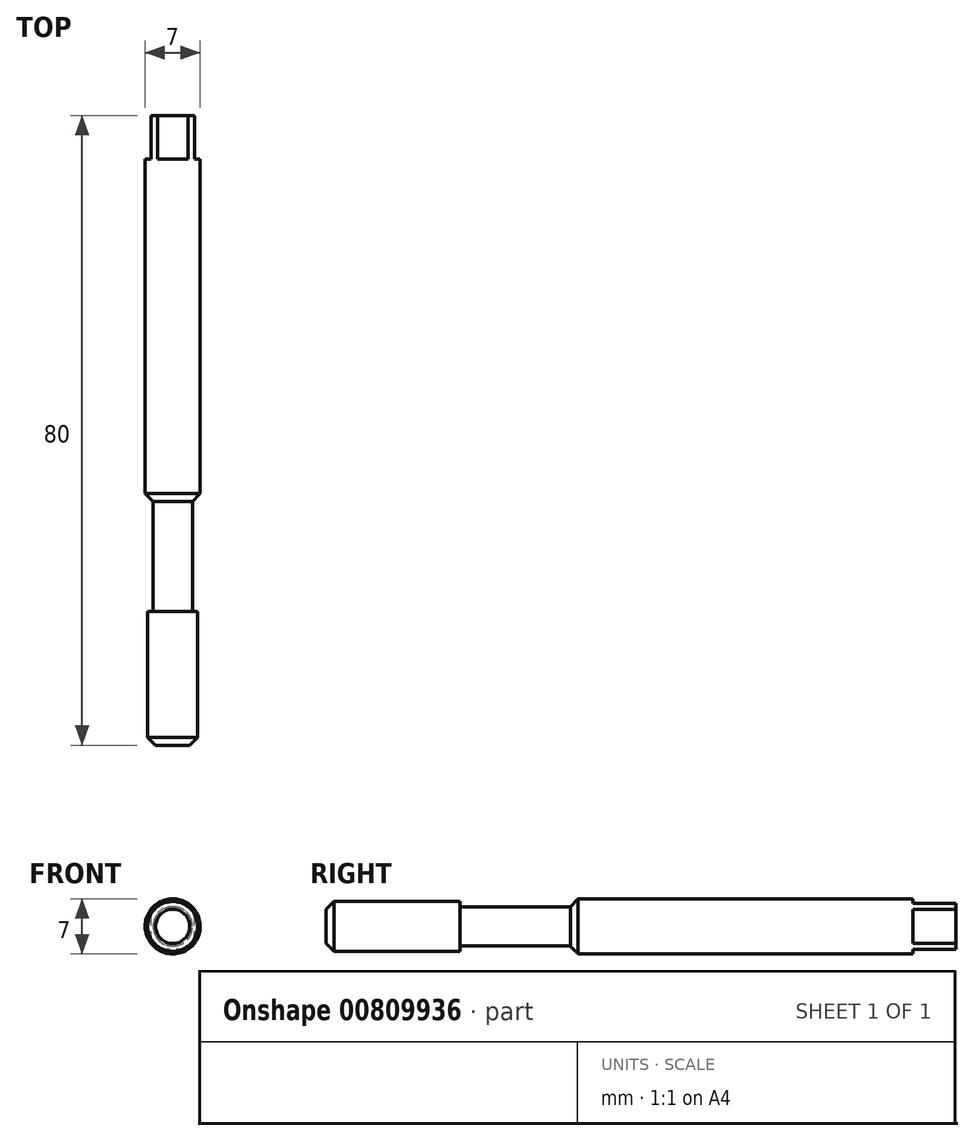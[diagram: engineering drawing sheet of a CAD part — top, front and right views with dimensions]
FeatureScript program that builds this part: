
annotation { "Feature Type Name" : "Feature", "Feature Type Description" : "" }
export const myFeature = defineFeature(function(context is Context, id is Id, definition is map)
    precondition{}
    {
        {
            var Q0;
            Q0=qCreatedBy(makeId("Front.planeOp"),FACE);
            var sketch = newSketch(context, id + "F0", { "sketchPlane" : qUnion([Q0])});
            skCircle(sketch, "E0", {"center": v(0, 0) * mm, "radius": 3.5 * mm});
            skSolve(sketch);
        }
        {
            var Q0;
            Q0 = qSketchRegion(id + "F0", true);
            extrude(context, id + "F1", {"entities" : qUnion([Q0]), "depth" : 80 * mm, "offsetDistance" : 25 * mm});
        }
        {
            var Q0;
            Q0=makeQuery(id+"F1.opExtrude","CAP_FACE",FACE,{"disambiguationData":[OSD([sQuery(id+"F0.wireOp",EDGE,"E0")])],"isStart":false});
            var sketch = newSketch(context, id + "F2", { "sketchPlane" : qUnion([Q0])});
            skCircle(sketch, "E1", {"center": v(0, 0) * mm, "radius": 2.5 * mm});
            skCircle(sketch, "E2", {"center": v(0, 0) * mm, "radius": 6.33 * mm});
            skSolve(sketch);
        }
        {
            var Q0;
            Q0 = qSketchRegion(id + "F2", true);
            extrude(context, id + "F3", {"entities" : qUnion([Q0]), "operationType" : NewBodyOperationType.REMOVE, "oppositeDirection" : true, "depth" : 30 * mm, "offsetDistance" : 25 * mm});
        }
        {
            var Q0;
            Q0=makeQuery(id+"F3.boolean.opBoolean","INTERSECT",EDGE,{"derivedFrom":[makeQuery(id+"F1.opExtrude","SWEPT_FACE",FACE,{"disambiguationData":[OSD([sQuery(id+"F0.wireOp",EDGE,"E0")])]}),makeQuery(id+"F3.opExtrude","CAP_FACE",FACE,{"disambiguationData":[OSD([sQuery(id+"F2.wireOp",EDGE,"E1"),sQuery(id+"F2.wireOp",EDGE,"E2")])],"isStart":false})]});
            chamfer(context, id + "F4", {"entities" : qUnion([Q0]), "width" : 2 * mm, "tangentPropagation" : true});
        }
        {
            var Q0;
            Q0=makeQuery(id+"F1.opExtrude","CAP_FACE",FACE,{"disambiguationData":[OSD([sQuery(id+"F0.wireOp",EDGE,"E0")])],"isStart":false});
            var sketch = newSketch(context, id + "F5", { "sketchPlane" : qUnion([Q0])});
            skCircle(sketch, "E3", {"center": v(0, 0) * mm, "radius": 3.17 * mm});
            skSolve(sketch);
        }
        {
            var Q0;
            Q0 = qSketchRegion(id + "F5", true);
            extrude(context, id + "F6", {"entities" : qUnion([Q0]), "operationType" : NewBodyOperationType.ADD, "oppositeDirection" : true, "depth" : 17 * mm, "offsetDistance" : 25 * mm});
        }
        {
            var Q0;
            Q0=makeQuery(id+"F6.opExtrude","CAP_EDGE",EDGE,{"disambiguationData":[OSD([sQuery(id+"F5.wireOp",EDGE,"E3")])],"isStart":true});
            chamfer(context, id + "F7", {"entities" : qUnion([Q0]), "width" : 1 * mm, "tangentPropagation" : true});
        }
        {
            var Q0;
            Q0=makeQuery(id+"F1.opExtrude","CAP_FACE",FACE,{"disambiguationData":[OSD([sQuery(id+"F0.wireOp",EDGE,"E0")])],"isStart":true});
            var sketch = newSketch(context, id + "F8", { "sketchPlane" : qUnion([Q0])});
            skLineSegment(sketch, "E4.bottom", {"start": v(-2.75, -2.9) * mm, "end": v(2.75, -2.9) * mm});
            skLineSegment(sketch, "E4.top", {"start": v(-2.75, 2.9) * mm, "end": v(2.75, 2.9) * mm});
            skLineSegment(sketch, "E4.left", {"start": v(-2.75, -2.9) * mm, "end": v(-2.75, 2.9) * mm});
            skLineSegment(sketch, "E4.right", {"start": v(2.75, -2.9) * mm, "end": v(2.75, 2.9) * mm});
            skPoint(sketch, "E4.middle", {"position": v(0, 0) * mm});
            skLineSegment(sketch, "E5.bottom", {"start": v(-4.86, -4) * mm, "end": v(4.86, -4) * mm});
            skLineSegment(sketch, "E5.top", {"start": v(-4.86, 4) * mm, "end": v(4.86, 4) * mm});
            skLineSegment(sketch, "E5.left", {"start": v(-4.86, -4) * mm, "end": v(-4.86, 4) * mm});
            skLineSegment(sketch, "E5.right", {"start": v(4.86, -4) * mm, "end": v(4.86, 4) * mm});
            skSolve(sketch);
        }
        {
            var Q0;
            Q0 = qSketchRegion(id + "F8", true);
            extrude(context, id + "F9", {"entities" : qUnion([Q0]), "operationType" : NewBodyOperationType.REMOVE, "oppositeDirection" : true, "depth" : 5.5 * mm, "offsetDistance" : 25 * mm});
        }
    });
